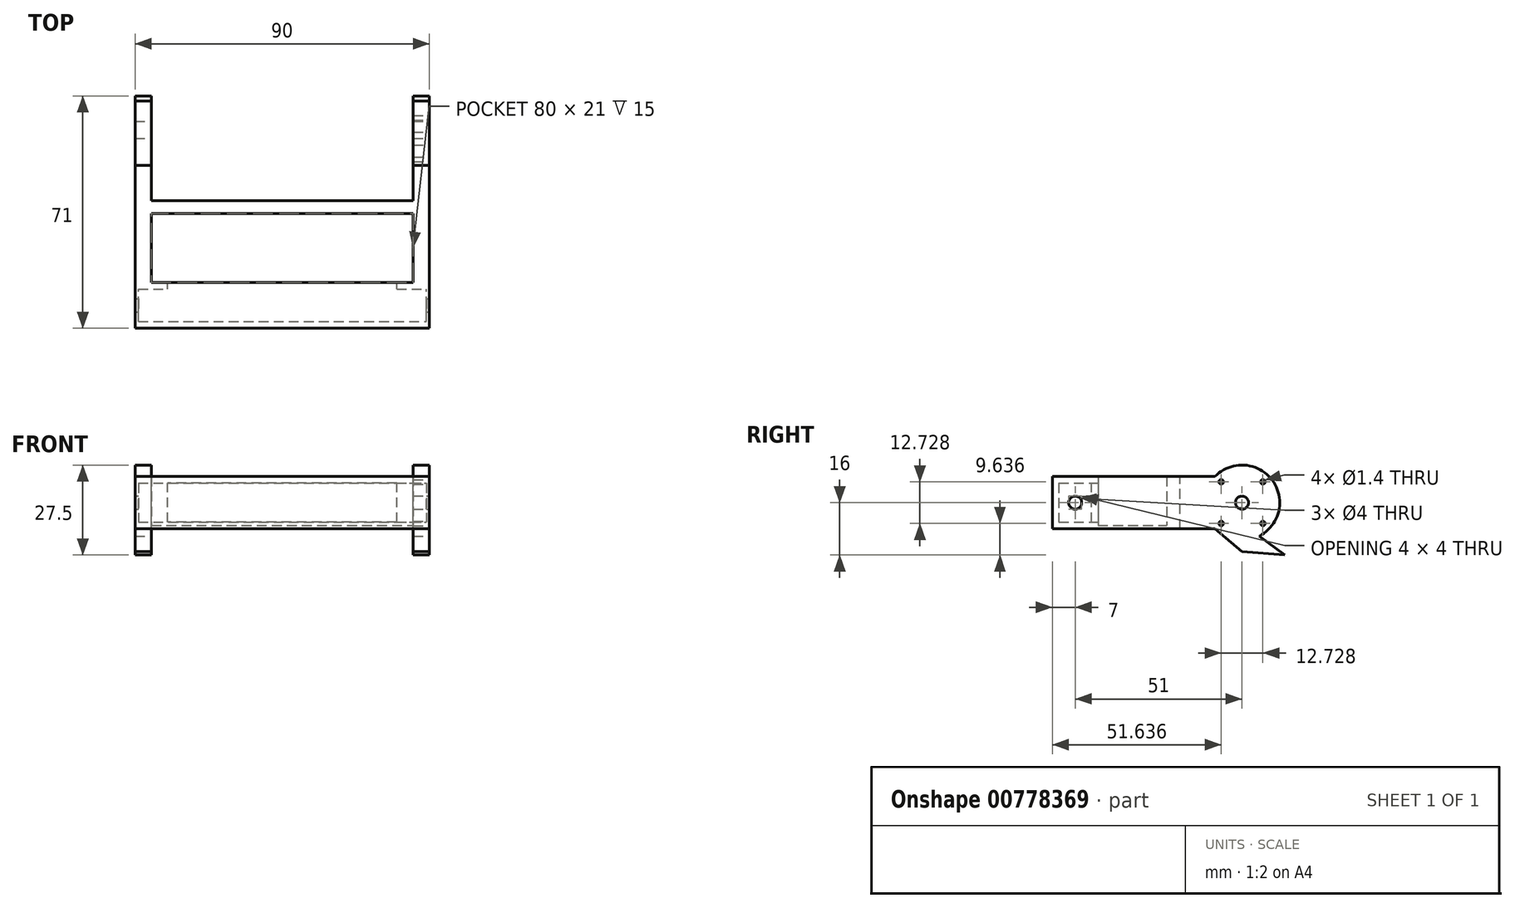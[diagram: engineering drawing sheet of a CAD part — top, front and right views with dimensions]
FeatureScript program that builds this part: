
annotation { "Feature Type Name" : "Feature", "Feature Type Description" : "" }
export const myFeature = defineFeature(function(context is Context, id is Id, definition is map)
    precondition{}
    {
        {
            var Q0;
            Q0=qCreatedBy(makeId("Top.planeOp"),FACE);
            var sketch = newSketch(context, id + "F0", { "sketchPlane" : qUnion([Q0])});
            skLineSegment(sketch, "E0.bottom", {"start": v(-45, -7) * mm, "end": v(45, -7) * mm});
            skLineSegment(sketch, "E0.top", {"start": v(-45, 67) * mm, "end": v(45, 67) * mm});
            skLineSegment(sketch, "E0.left", {"start": v(-45, -7) * mm, "end": v(-45, 67) * mm});
            skLineSegment(sketch, "E0.right", {"start": v(45, -7) * mm, "end": v(45, 67) * mm});
            skSolve(sketch);
        }
        {
            var Q0;
            Q0=makeQuery(id+"F0.imprint","IMPRINT",FACE,{"disambiguationData":[TD([[makeQuery(id+"F0.imprint","IMPRINT",EDGE,{"derivedFrom":sQuery(id+"F0.wireOp",EDGE,"E0.bottom")}),1.0]])]});
            extrude(context, id + "F1", {"entities" : qUnion([Q0]), "endBound" : BoundingType.SYMMETRIC, "depth" : 16 * mm, "offsetDistance" : 25 * mm});
        }
        {
            var Q0;
            Q0=qCreatedBy(makeId("Right.planeOp"),FACE);
            var sketch = newSketch(context, id + "F2", { "sketchPlane" : qUnion([Q0])});
            skLineSegment(sketch, "E1.bottom", {"start": v(-5, 6) * mm, "end": v(5, 6) * mm});
            skLineSegment(sketch, "E1.top", {"start": v(-5, -6) * mm, "end": v(5, -6) * mm});
            skLineSegment(sketch, "E1.left", {"start": v(-5, 6) * mm, "end": v(-5, -6) * mm});
            skLineSegment(sketch, "E1.right", {"start": v(5, 6) * mm, "end": v(5, -6) * mm});
            skSolve(sketch);
        }
        {
            var Q0;
            Q0 = qSketchRegion(id + "F2", true);
            extrude(context, id + "F3", {"entities" : qUnion([Q0]), "operationType" : NewBodyOperationType.REMOVE, "endBound" : BoundingType.SYMMETRIC, "oppositeDirection" : true, "depth" : 88 * mm, "offsetDistance" : 25 * mm});
        }
        {
            var Q0;
            Q0=qCreatedBy(makeId("Top.planeOp"),FACE);
            var sketch = newSketch(context, id + "F4", { "sketchPlane" : qUnion([Q0])});
            skLineSegment(sketch, "E2.bottom", {"start": v(-40, 7) * mm, "end": v(40, 7) * mm});
            skLineSegment(sketch, "E2.top", {"start": v(-40, 28) * mm, "end": v(40, 28) * mm});
            skLineSegment(sketch, "E2.left", {"start": v(-40, 7) * mm, "end": v(-40, 28) * mm});
            skLineSegment(sketch, "E2.right", {"start": v(40, 7) * mm, "end": v(40, 28) * mm});
            skSolve(sketch);
        }
        {
            var Q0;
            Q0 = qSketchRegion(id + "F4", true);
            extrude(context, id + "F5", {"entities" : qUnion([Q0]), "operationType" : NewBodyOperationType.REMOVE, "depth" : 25 * mm, "offsetDistance" : 25 * mm});
        }
        {
            var Q0;
            Q0 = qSketchRegion(id + "F4", true);
            extrude(context, id + "F6", {"entities" : qUnion([Q0]), "operationType" : NewBodyOperationType.REMOVE, "oppositeDirection" : true, "depth" : 7 * mm, "offsetDistance" : 25 * mm});
        }
        {
            var Q0;
            {var subQ0=sQuery(id+"F4.wireOp",EDGE,"E2.bottom");Q0=makeQuery(id+"F6.boolean.opBoolean","MERGE",FACE,{"derivedFrom":[makeQuery(id+"F5.boolean.opBoolean","COPY",FACE,{"derivedFrom":makeQuery(id+"F5.opExtrude","SWEPT_FACE",FACE,{"disambiguationData":[OSD([subQ0])]})}),makeQuery(id+"F6.opExtrude","SWEPT_FACE",FACE,{"disambiguationData":[OSD([subQ0])]})]});}
            var sketch = newSketch(context, id + "F7", { "sketchPlane" : qUnion([Q0])});
            skLineSegment(sketch, "E3.bottom", {"start": v(-35, 6) * mm, "end": v(35, 6) * mm});
            skLineSegment(sketch, "E3.top", {"start": v(-35, -6) * mm, "end": v(35, -6) * mm});
            skLineSegment(sketch, "E3.left", {"start": v(-35, 6) * mm, "end": v(-35, -6) * mm});
            skLineSegment(sketch, "E3.right", {"start": v(35, 6) * mm, "end": v(35, -6) * mm});
            skSolve(sketch);
        }
        {
            var Q0;
            Q0 = qSketchRegion(id + "F7", true);
            extrude(context, id + "F8", {"entities" : qUnion([Q0]), "operationType" : NewBodyOperationType.REMOVE, "oppositeDirection" : true, "depth" : 3 * mm, "offsetDistance" : 25 * mm});
        }
        {
            var Q0;
            Q0=qCreatedBy(makeId("Right.planeOp"),FACE);
            var sketch = newSketch(context, id + "F9", { "sketchPlane" : qUnion([Q0])});
            skCircle(sketch, "E4", {"center": v(0, 0) * mm, "radius": 2 * mm});
            skSolve(sketch);
        }
        {
            var Q0;
            Q0 = qSketchRegion(id + "F9", true);
            extrude(context, id + "F10", {"entities" : qUnion([Q0]), "operationType" : NewBodyOperationType.REMOVE, "endBound" : BoundingType.SYMMETRIC, "oppositeDirection" : true, "depth" : 100 * mm, "offsetDistance" : 25 * mm});
        }
        {
            var Q0;
            Q0=makeQuery(id+"F1.opExtrude","CAP_FACE",FACE,{"disambiguationData":[OSD([sQuery(id+"F0.wireOp",EDGE,"E0.bottom"),sQuery(id+"F0.wireOp",EDGE,"E0.top"),sQuery(id+"F0.wireOp",EDGE,"E0.left"),sQuery(id+"F0.wireOp",EDGE,"E0.right")])],"isStart":false});
            var sketch = newSketch(context, id + "F11", { "sketchPlane" : qUnion([Q0])});
            skLineSegment(sketch, "E5.bottom", {"start": v(-40, 32) * mm, "end": v(40, 32) * mm});
            skLineSegment(sketch, "E5.top", {"start": v(-40, 70) * mm, "end": v(40, 70) * mm});
            skLineSegment(sketch, "E5.left", {"start": v(-40, 32) * mm, "end": v(-40, 70) * mm});
            skLineSegment(sketch, "E5.right", {"start": v(40, 32) * mm, "end": v(40, 70) * mm});
            skSolve(sketch);
        }
        {
            var Q0;
            Q0 = qSketchRegion(id + "F11", true);
            extrude(context, id + "F12", {"entities" : qUnion([Q0]), "operationType" : NewBodyOperationType.REMOVE, "oppositeDirection" : true, "depth" : 25 * mm, "offsetDistance" : 25 * mm});
        }
        {
            var Q0;
            Q0=makeQuery(id+"F1.opExtrude","SWEPT_FACE",FACE,{"disambiguationData":[OSD([sQuery(id+"F0.wireOp",EDGE,"E0.right")])]});
            var sketch = newSketch(context, id + "F13", { "sketchPlane" : qUnion([Q0])});
            skCircle(sketch, "E6", {"center": v(51, 0) * mm, "radius": 2 * mm});
            skCircle(sketch, "E7.1.0", {"center": v(44.64, 6.36) * mm, "radius": 0.7 * mm});
            skLineSegment(sketch, "E7.anchor1", {"start": v(51, 0) * mm, "end": v(51, 9) * mm, "construction": true});
            skLineSegment(sketch, "E7.anchor2", {"start": v(51, 0) * mm, "end": v(42, 0) * mm, "construction": true});
            skCircle(sketch, "E8.1.0", {"center": v(57.36, 6.36) * mm, "radius": 0.7 * mm});
            skLineSegment(sketch, "E8.anchor2", {"start": v(51, 0) * mm, "end": v(60, 0) * mm, "construction": true});
            skCircle(sketch, "E9.MirrorC", {"center": v(44.64, -6.36) * mm, "radius": 0.7 * mm});
            skCircle(sketch, "E10.MirrorC", {"center": v(57.36, -6.36) * mm, "radius": 0.7 * mm});
            skSolve(sketch);
        }
        {
            var Q0;
            Q0 = qSketchRegion(id + "F13", true);
            extrude(context, id + "F14", {"entities" : qUnion([Q0]), "operationType" : NewBodyOperationType.REMOVE, "oppositeDirection" : true, "depth" : 25 * mm, "offsetDistance" : 25 * mm});
        }
        {
            var Q0;
            Q0=makeQuery(id+"F1.opExtrude","CAP_FACE",FACE,{"disambiguationData":[OSD([sQuery(id+"F0.wireOp",EDGE,"E0.bottom"),sQuery(id+"F0.wireOp",EDGE,"E0.top"),sQuery(id+"F0.wireOp",EDGE,"E0.left"),sQuery(id+"F0.wireOp",EDGE,"E0.right")])],"isStart":false});
            var sketch = newSketch(context, id + "F15", { "sketchPlane" : qUnion([Q0])});
            skLineSegment(sketch, "E11.bottom", {"start": v(45, 67) * mm, "end": v(40, 67) * mm});
            skLineSegment(sketch, "E11.top", {"start": v(45, 32) * mm, "end": v(40, 32) * mm});
            skLineSegment(sketch, "E11.left", {"start": v(45, 67) * mm, "end": v(45, 32) * mm});
            skLineSegment(sketch, "E11.right", {"start": v(40, 67) * mm, "end": v(40, 32) * mm});
            skLineSegment(sketch, "E12.bottom", {"start": v(-40, 32) * mm, "end": v(-45, 32) * mm});
            skLineSegment(sketch, "E12.top", {"start": v(-40, 67) * mm, "end": v(-45, 67) * mm});
            skLineSegment(sketch, "E12.left", {"start": v(-40, 32) * mm, "end": v(-40, 67) * mm});
            skLineSegment(sketch, "E12.right", {"start": v(-45, 32) * mm, "end": v(-45, 67) * mm});
            skSolve(sketch);
        }
        {
            var Q0;
            Q0 = qSketchRegion(id + "F15", true);
            extrude(context, id + "F16", {"entities" : qUnion([Q0]), "operationType" : NewBodyOperationType.ADD, "depth" : 5 * mm, "offsetDistance" : 25 * mm});
        }
        {
            var Q0;
            Q0=makeQuery(id+"F1.opExtrude","CAP_FACE",FACE,{"disambiguationData":[OSD([sQuery(id+"F0.wireOp",EDGE,"E0.bottom"),sQuery(id+"F0.wireOp",EDGE,"E0.top"),sQuery(id+"F0.wireOp",EDGE,"E0.left"),sQuery(id+"F0.wireOp",EDGE,"E0.right")])],"isStart":true});
            var sketch = newSketch(context, id + "F17", { "sketchPlane" : qUnion([Q0])});
            skLineSegment(sketch, "E13.bottom", {"start": v(40, -32) * mm, "end": v(45, -32) * mm});
            skLineSegment(sketch, "E13.top", {"start": v(40, -67) * mm, "end": v(45, -67) * mm});
            skLineSegment(sketch, "E13.left", {"start": v(40, -32) * mm, "end": v(40, -67) * mm});
            skLineSegment(sketch, "E13.right", {"start": v(45, -32) * mm, "end": v(45, -67) * mm});
            skLineSegment(sketch, "E14.bottom", {"start": v(-40, -32) * mm, "end": v(-45, -32) * mm});
            skLineSegment(sketch, "E14.top", {"start": v(-40, -67) * mm, "end": v(-45, -67) * mm});
            skLineSegment(sketch, "E14.left", {"start": v(-40, -32) * mm, "end": v(-40, -67) * mm});
            skLineSegment(sketch, "E14.right", {"start": v(-45, -32) * mm, "end": v(-45, -67) * mm});
            skSolve(sketch);
        }
        {
            var Q0;
            Q0 = qSketchRegion(id + "F17", true);
            extrude(context, id + "F18", {"entities" : qUnion([Q0]), "operationType" : NewBodyOperationType.ADD, "depth" : 20 * mm, "offsetDistance" : 25 * mm});
        }
        {
            var Q0;
            Q0=qCreatedBy(makeId("Right.planeOp"),FACE);
            var sketch = newSketch(context, id + "F19", { "sketchPlane" : qUnion([Q0])});
            skCircle(sketch, "E15", {"center": v(0, 0) * mm, "radius": 16 * mm, "construction": true});
            skCircle(sketch, "E16", {"center": v(51, 0) * mm, "radius": 16 * mm, "construction": true});
            skLineSegment(sketch, "E17", {"start": v(64, -16) * mm, "end": v(51, -15) * mm});
            skArc(sketch, "E18", {"start": v(56.3, -10.2) * mm, "mid": v(60.22, 6.87) * mm, "end": v(42.74, 8) * mm});
            skLineSegment(sketch, "E19", {"start": v(30.44, 8) * mm, "end": v(42.74, 8) * mm});
            skLineSegment(sketch, "E20", {"start": v(30.1, -8) * mm, "end": v(42.74, -8) * mm});
            skLineSegment(sketch, "E21", {"start": v(64, -16) * mm, "end": v(56.3, -10.2) * mm});
            skLineSegment(sketch, "E22", {"start": v(64, -16) * mm, "end": v(51, -16) * mm, "construction": true});
            skLineSegment(sketch, "E23", {"start": v(42.74, -8) * mm, "end": v(51, -15) * mm});
            skLineSegment(sketch, "E24", {"start": v(30.44, 8) * mm, "end": v(30.44, 17.84) * mm});
            skLineSegment(sketch, "E25", {"start": v(30.44, 17.84) * mm, "end": v(73.1, 17.13) * mm});
            skLineSegment(sketch, "E26", {"start": v(73.1, 17.13) * mm, "end": v(71.44, -31) * mm});
            skLineSegment(sketch, "E27", {"start": v(71.44, -31) * mm, "end": v(30.1, -29.58) * mm});
            skLineSegment(sketch, "E28", {"start": v(30.1, -29.58) * mm, "end": v(30.1, -8) * mm});
            skSolve(sketch);
        }
        {
            var Q0;
            Q0 = qSketchRegion(id + "F19", true);
            extrude(context, id + "F20", {"entities" : qUnion([Q0]), "operationType" : NewBodyOperationType.REMOVE, "endBound" : BoundingType.SYMMETRIC, "oppositeDirection" : true, "depth" : 100 * mm, "offsetDistance" : 25 * mm});
        }
    });
